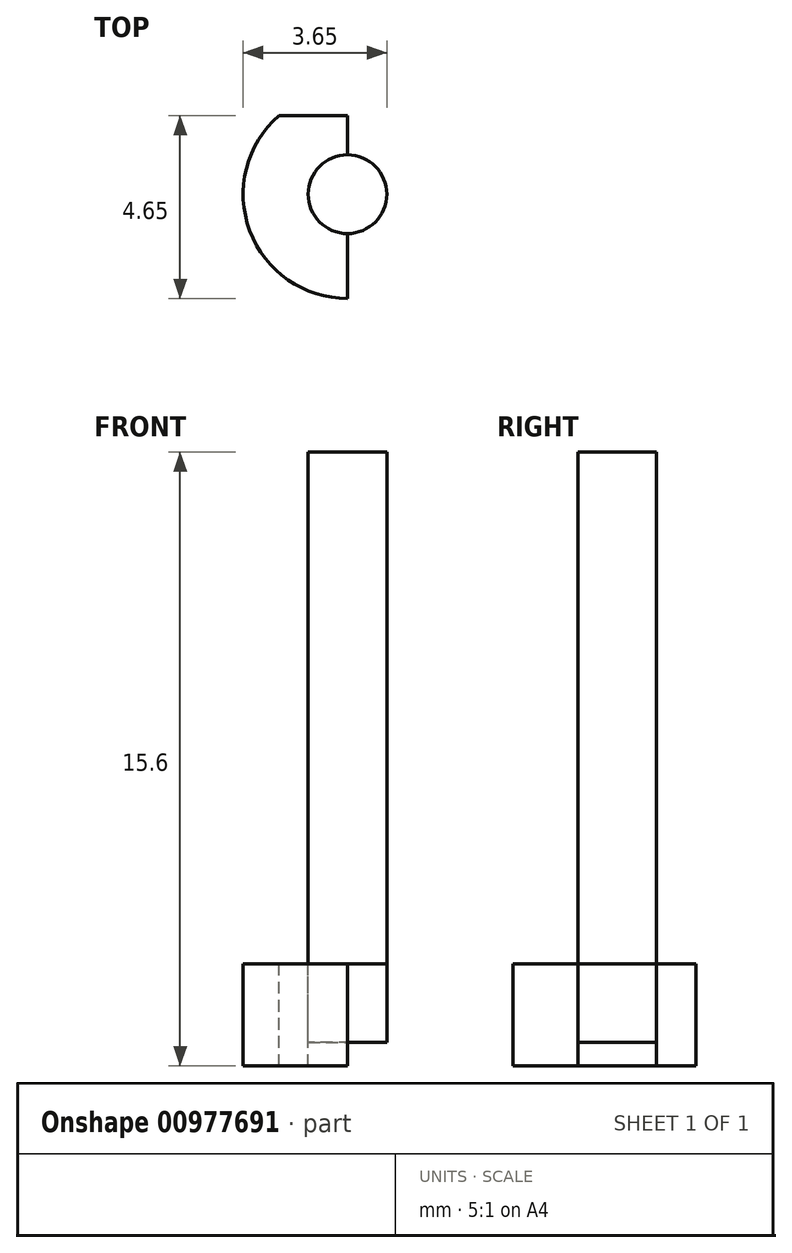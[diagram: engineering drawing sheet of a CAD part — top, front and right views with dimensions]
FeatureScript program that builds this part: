
annotation { "Feature Type Name" : "Feature", "Feature Type Description" : "" }
export const myFeature = defineFeature(function(context is Context, id is Id, definition is map)
    precondition{}
    {
        {
            var Q0;
            Q0=qCreatedBy(makeId("Top.planeOp"),FACE);
            var sketch = newSketch(context, id + "F0", { "sketchPlane" : qUnion([Q0])});
            skCircle(sketch, "E0", {"center": v(0, 0) * mm, "radius": 2.65 * mm});
            skLineSegment(sketch, "E1", {"start": v(0, -2.65) * mm, "end": v(0, 2) * mm});
            skLineSegment(sketch, "E2", {"start": v(0, 2) * mm, "end": v(1.74, 2) * mm});
            skLineSegment(sketch, "E3", {"start": v(1.74, 2) * mm, "end": v(0, 2) * mm});
            skLineSegment(sketch, "E4", {"start": v(0, 2) * mm, "end": v(-1.74, 2) * mm});
            skCircle(sketch, "E5", {"center": v(0, 0) * mm, "radius": 1 * mm});
            skSolve(sketch);
        }
        {
            var Q0;
            {var subQ0=sQuery(id+"F0.wireOp",EDGE,"E3");Q0=makeQuery(id+"F0.imprint","IMPRINT",FACE,{"disambiguationData":[TD([[makeQuery(id+"F0.imprint","IMPRINT",EDGE,{"derivedFrom":subQ0}),1.0]])]});}
            var Q1;
            {var subQ0=sQuery(id+"F0.wireOp",EDGE,"E4");Q1=makeQuery(id+"F0.imprint","IMPRINT",FACE,{"disambiguationData":[TD([[makeQuery(id+"F0.imprint","IMPRINT",EDGE,{"derivedFrom":subQ0}),1.0]])]});}
            extrude(context, id + "F1", {"entities" : qUnion([Q0, Q1]), "oppositeDirection" : true, "depth" : 2.6 * mm, "offsetDistance" : 25 * mm});
        }
        {
            var Q0;
            {var subQ0=sQuery(id+"F0.wireOp",EDGE,"E5");var subQ1=sQuery(id+"F0.wireOp",EDGE,"E1");var subQ2=makeQuery(id+"F0.imprint","INTERSECT",VERTEX,{"disambiguationData":[OD(0.0)],"derivedFrom":[subQ1,subQ0]});Q0=makeQuery(id+"F0.imprint","IMPRINT",FACE,{"disambiguationData":[TD([[makeQuery(id+"F0.imprint","IMPRINT",EDGE,{"disambiguationData":[TD([[subQ2,-1.0]])],"derivedFrom":subQ1}),1.0]])]});}
            var Q1;
            {var subQ0=sQuery(id+"F0.wireOp",EDGE,"E5");var subQ1=sQuery(id+"F0.wireOp",EDGE,"E1");var subQ2=makeQuery(id+"F0.imprint","INTERSECT",VERTEX,{"disambiguationData":[OD(0.0)],"derivedFrom":[subQ1,subQ0]});Q1=makeQuery(id+"F0.imprint","IMPRINT",FACE,{"disambiguationData":[TD([[makeQuery(id+"F0.imprint","IMPRINT",EDGE,{"disambiguationData":[TD([[subQ2,-1.0]])],"derivedFrom":subQ1}),-1.0]])]});}
            extrude(context, id + "F2", {"entities" : qUnion([Q0, Q1]), "depth" : 13 * mm, "offsetDistance" : 25 * mm});
        }
        {
            var Q0;
            Q0=makeQuery(id+"F2.opExtrude","CAP_FACE",FACE,{"disambiguationData":[OSD([sQuery(id+"F0.wireOp",EDGE,"E5")])],"isStart":true});
            extrude(context, id + "F3", {"entities" : qUnion([Q0]), "depth" : 2 * mm, "offsetDistance" : 25 * mm});
        }
    });
